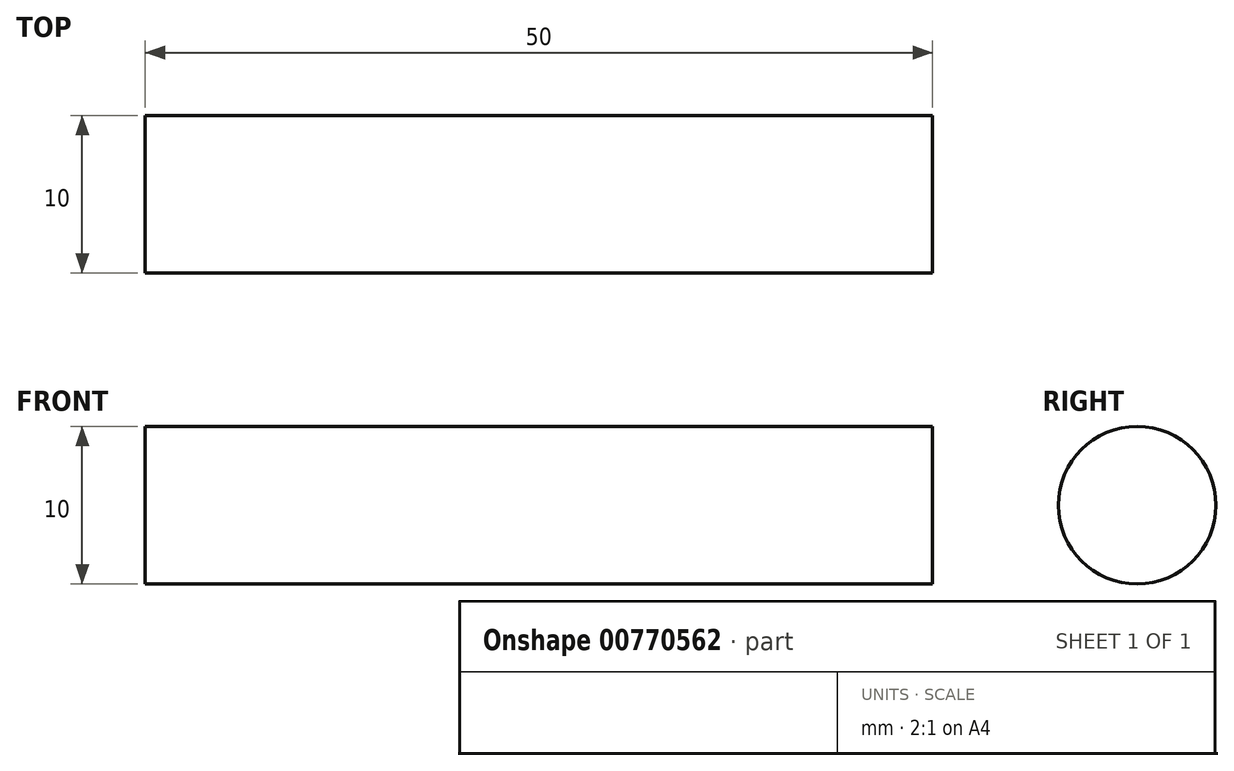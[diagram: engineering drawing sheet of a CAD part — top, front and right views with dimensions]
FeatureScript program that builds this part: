
annotation { "Feature Type Name" : "Feature", "Feature Type Description" : "" }
export const myFeature = defineFeature(function(context is Context, id is Id, definition is map)
    precondition{}
    {
        {
            var Q0;
            Q0=qCreatedBy(makeId("Right.planeOp"),FACE);
            var sketch = newSketch(context, id + "F0", { "sketchPlane" : qUnion([Q0])});
            skCircle(sketch, "E0", {"center": v(0, 0) * mm, "radius": 5 * mm});
            skSolve(sketch);
        }
        {
            var Q0;
            Q0 = qSketchRegion(id + "F0", true);
            extrude(context, id + "F1", {"entities" : qUnion([Q0]), "depth" : 50 * mm, "offsetDistance" : 25 * mm});
        }
    });
